# Revit family: CENTUM Einzel-Rollenlager
name_source: partatom
category: HLS-Bauteile
revit_build: Autodesk Revit 2017 (Build: 20190507_1515(x64)
units: mm (PartAtom-declared; Revit-internal decimal feet)

## family parameters
Arbeitsebenenbasiert = Ja
Beim Laden mit Abzugskörper schneiden = Nein
Bemaßung runder Anschluss = Durchmesser verwenden
Gemeinsam genutzt = Ja
Immer vertikal = Nein
Raumberechnungspunkt = Nein
Teiletyp = Normal

## types (12) — shared parameters
Fabrikat = MEFA
Firma = MEFA Befestigungs- und Montagesysteme GmbH
Kurztext1 = Rollenlager einzel axial
Material = Stahl
Materialname = S235
Mengeneinheit = St
Sicherheitsfaktor = 1.54
Vorgabe-Ansicht = 1219 mm
vpe = 1 St

## per-type parameters (varying)
| type | Artikelnummer | EAN | Einzel-Rollenlager | Gewicht | Gewicht pro Bauteil | Höhe | Kurztext2 | Lochabstand längs | Lochabstand quer | Lochdurchmesser | Länge | Oberflaeche | Rollenbreite | Stärke Material | max. zul. Last |
| Einzel-Rollenlager  70, fvz | 150sf060070 | 4250928435347 | MEFA Einzel-Rollenlager  70 | 1.00 kg | 1.00 kg | 50 mm | Rollenbreite 70 mm fsv | 50 mm  [stored 0.164042 ft] | 45 mm  [stored 0.147638 ft] | 8 mm | 94 mm  [stored 0.308399 ft] | feuerstückverzinkt | 70 mm | 6 mm  [stored 0.019685 ft] | 5.00 kN |
| Einzel-Rollenlager  70, gvz | 150sg060070 | 4250928435385 | MEFA Einzel-Rollenlager  70 | 1.00 kg | 1.00 kg | 50 mm | Rollenbreite 70 mm gvz | 50 mm  [stored 0.164042 ft] | 45 mm  [stored 0.147638 ft] | 8 mm | 94 mm  [stored 0.308399 ft] | galvanisch verzinkt | 70 mm | 6 mm  [stored 0.019685 ft] | 5.00 kN |
| Einzel-Rollenlager  70, roh | 150sr060070 | 4250928435422 | MEFA Einzel-Rollenlager  70 | 1.00 kg | 1.00 kg | 50 mm | Rollenbreite 70 mm roh | 50 mm  [stored 0.164042 ft] | 45 mm  [stored 0.147638 ft] | 8 mm | 94 mm  [stored 0.308399 ft] | roh | 70 mm | 6 mm  [stored 0.019685 ft] | 5.00 kN |
| Einzel-Rollenlager 100, fvz | 150sf080100 | 4250928435354 | MEFA Einzel-Rollenlager 100 | 3.40 kg | 3.40 kg | 75 mm | Rollenbreite 100 mm fsv | 60 mm  [stored 0.19685 ft] | 60 mm  [stored 0.19685 ft] | 10 mm | 126 mm  [stored 0.413386 ft] | feuerstückverzinkt | 100 mm | 10 mm  [stored 0.0328084 ft] | 15.00 kN |
| Einzel-Rollenlager 100, gvz | 150sg080100 | 4250928435392 | MEFA Einzel-Rollenlager 100 | 3.40 kg | 3.40 kg | 75 mm | Rollenbreite 100 mm gvz | 60 mm  [stored 0.19685 ft] | 60 mm  [stored 0.19685 ft] | 10 mm | 126 mm  [stored 0.413386 ft] | galvanisch verzinkt | 100 mm | 10 mm  [stored 0.0328084 ft] | 15.00 kN |
| Einzel-Rollenlager 100, roh | 150sr080100 | 4250928435439 | MEFA Einzel-Rollenlager 100 | 3.40 kg | 3.40 kg | 75 mm | Rollenbreite 100 mm roh | 60 mm  [stored 0.19685 ft] | 60 mm  [stored 0.19685 ft] | 10 mm | 126 mm  [stored 0.413386 ft] | roh | 100 mm | 10 mm  [stored 0.0328084 ft] | 15.00 kN |
| Einzel-Rollenlager 140, fvz | 150sf100140 | 4250928435361 | MEFA Einzel-Rollenlager 140 | 5.00 kg | 5.00 kg | 90 mm | Rollenbreite 140 mm fsv | 80 mm  [stored 0.262467 ft] | 80 mm  [stored 0.262467 ft] | 12 mm | 172 mm  [stored 0.564304 ft] | feuerstückverzinkt | 140 mm | 10 mm  [stored 0.0328084 ft] | 25.00 kN |
| Einzel-Rollenlager 140, gvz | 150sg100140 | 4250928435408 | MEFA Einzel-Rollenlager 140 | 7.52 kg | 7.52 kg | 90 mm | Rollenbreite 140 mm gvz | 80 mm  [stored 0.262467 ft] | 80 mm  [stored 0.262467 ft] | 12 mm | 172 mm  [stored 0.564304 ft] | galvanisch verzinkt | 140 mm | 10 mm  [stored 0.0328084 ft] | 25.00 kN |
| Einzel-Rollenlager 140, roh | 150sr100140 | 4250928435446 | MEFA Einzel-Rollenlager 140 | 5.00 kg | 5.00 kg | 90 mm | Rollenbreite 140 mm roh | 80 mm  [stored 0.262467 ft] | 80 mm  [stored 0.262467 ft] | 12 mm | 172 mm  [stored 0.564304 ft] | roh | 140 mm | 10 mm  [stored 0.0328084 ft] | 25.00 kN |
| Einzel-Rollenlager 170, fvz | 150sf130170 | 4250928435378 | MEFA Einzel-Rollenlager 170 | 14.00 kg | 14.00 kg | 125 mm | Rollenbreite 170 mm fsv | 100 mm  [stored 0.328084 ft] | 100 mm  [stored 0.328084 ft] | 14 mm | 218 mm  [stored 0.715223 ft] | feuerstückverzinkt | 170 mm | 12 mm  [stored 0.0393701 ft] | 50.00 kN |
| Einzel-Rollenlager 170, gvz | 150sg130170 | 4250928435415 | MEFA Einzel-Rollenlager 170 | 14.00 kg | 14.00 kg | 125 mm | Rollenbreite 170 mm gvz | 100 mm  [stored 0.328084 ft] | 100 mm  [stored 0.328084 ft] | 14 mm | 218 mm  [stored 0.715223 ft] | galvanisch verzinkt | 170 mm | 12 mm  [stored 0.0393701 ft] | 50.00 kN |
| Einzel-Rollenlager 170, roh | 150sr130170 | 4250928435453 | MEFA Einzel-Rollenlager 170 | 14.00 kg | 14.00 kg | 125 mm | Rollenbreite 170 mm roh | 100 mm  [stored 0.328084 ft] | 100 mm  [stored 0.328084 ft] | 14 mm | 218 mm  [stored 0.715223 ft] | roh | 170 mm | 12 mm  [stored 0.0393701 ft] | 50.00 kN |

note: [stored X ft] marks values corroborated as IEEE doubles in the binary element streams (Revit-internal decimal feet)
